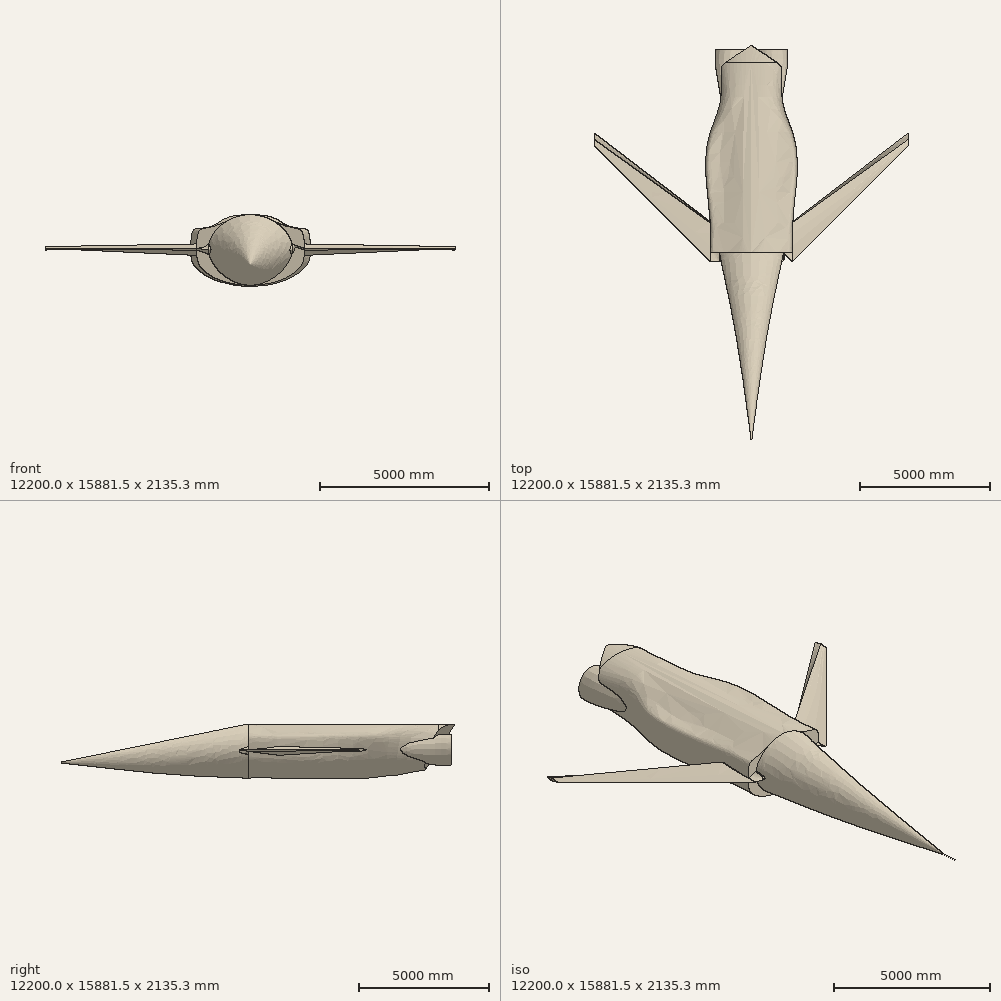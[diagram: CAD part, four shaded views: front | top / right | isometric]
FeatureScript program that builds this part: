
annotation { "Feature Type Name" : "Feature", "Feature Type Description" : "" }
export const myFeature = defineFeature(function(context is Context, id is Id, definition is map)
    precondition{}
    {
        {
            var Q0;
            Q0=qCreatedBy(makeId("Right.planeOp"),FACE);
            var sketch = newSketch(context, id + "F0", { "sketchPlane" : qUnion([Q0])});
            skLineSegment(sketch, "E0", {"start": v(0, 0) * mm, "end": v(-1750, 0) * mm});
            skLineSegment(sketch, "E1", {"start": v(-1750, 0) * mm, "end": v(-3500, 0) * mm});
            skLineSegment(sketch, "E2", {"start": v(-3500, 0) * mm, "end": v(-3500, -1000) * mm});
            skLineSegment(sketch, "E3", {"start": v(-3500, -1000) * mm, "end": v(-8500, -1000) * mm});
            skLineSegment(sketch, "E4", {"start": v(-8500, -1000) * mm, "end": v(-8500, -499.31) * mm});
            skLineSegment(sketch, "E5", {"start": v(-1151.4, 0) * mm, "end": v(-1151.4, 1000) * mm});
            skLineSegment(sketch, "E6", {"start": v(-1151.4, 1000) * mm, "end": v(-8500, -499.31) * mm});
            skLineSegment(sketch, "E7", {"start": v(-8500, -499.31) * mm, "end": v(-3500, -1000) * mm});
            skLineSegment(sketch, "E8", {"start": v(-3500, 0) * mm, "end": v(-3500, 520.82) * mm});
            skLineSegment(sketch, "E9", {"start": v(-8500, -499.31) * mm, "end": v(-8450, -499.31) * mm});
            skLineSegment(sketch, "E10", {"start": v(-8450, -499.31) * mm, "end": v(-8450, -489.1) * mm});
            skLineSegment(sketch, "E11", {"start": v(-8450, -499.31) * mm, "end": v(-8450, -504.32) * mm});
            skSolve(sketch);
        }
        {
            var Q0;
            Q0=sQuery(id+"F0.wireOp",EDGE,"E5");
            cPlane(context, id + "F1", {"entities" : qUnion([Q0]), "cplaneType" : CPlaneType.LINE_ANGLE, "offset" : 25 * mm, "angle" : 90 * degree, "oppositeDirection" : true, "width" : 150 * mm, "height" : 150 * mm});
        }
        {
            var Q0;
            Q0=qCreatedBy(id+"F1.planeOp",FACE);
            var sketch = newSketch(context, id + "F2", { "sketchPlane" : qUnion([Q0])});
            skPoint(sketch, "E12.middle", {"position": v(0, 0) * mm});
            skFitSpline(sketch, "E13", {"points": [v(0, 1000) * mm, v(-1060, 662.5) * mm, v(-1517.6, 506.84) * mm, v(-1600, 0) * mm, v(-1517.6, -506.84) * mm, v(-750, -1000) * mm, v(750, -1000) * mm, v(1517.6, -506.84) * mm, v(1600, 0) * mm, v(1517.6, 506.84) * mm, v(1060, 662.5) * mm, v(0, 1000) * mm]});
            skSolve(sketch);
        }
        {
            var Q0;
            Q0=qCreatedBy(makeId("Front.planeOp"),FACE);
            var sketch = newSketch(context, id + "F3", { "sketchPlane" : qUnion([Q0])});
            skPoint(sketch, "E14.middle", {"position": v(0, 0) * mm});
            skFitSpline(sketch, "E15", {"points": [v(0, 1000) * mm, v(-1060, 662.5) * mm, v(-1517.6, 506.84) * mm, v(-1600, 0) * mm, v(-1517.6, -506.84) * mm, v(-750, -1000) * mm, v(750, -1000) * mm, v(1517.6, -506.84) * mm, v(1600, 0) * mm, v(1517.6, 506.84) * mm, v(1060, 662.5) * mm, v(0, 1000) * mm]});
            skSolve(sketch);
        }
        {
            var Q0;
            Q0=qCreatedBy(makeId("Front.planeOp"),FACE);
            cPlane(context, id + "F4", {"entities" : qUnion([Q0]), "cplaneType" : CPlaneType.OFFSET, "offset" : 3500 * mm, "oppositeDirection" : true, "width" : 150 * mm, "height" : 150 * mm});
        }
        {
            var Q0;
            Q0=qCreatedBy(id+"F4.planeOp",FACE);
            var sketch = newSketch(context, id + "F5", { "sketchPlane" : qUnion([Q0])});
            skPoint(sketch, "E16.middle", {"position": v(0, 0) * mm});
            skFitSpline(sketch, "E17", {"points": [v(0, 1000) * mm, v(-1060, 662.5) * mm, v(-1517.6, 506.84) * mm, v(-1600, 0) * mm, v(-1517.6, -506.84) * mm, v(-750, -1000) * mm, v(750, -1000) * mm, v(1517.6, -506.84) * mm, v(1600, 0) * mm, v(1517.6, 506.84) * mm, v(1060, 662.5) * mm, v(0, 1000) * mm]});
            skSolve(sketch);
        }
        {
            var Q0;
            Q0=qCreatedBy(makeId("Front.planeOp"),FACE);
            cPlane(context, id + "F6", {"entities" : qUnion([Q0]), "cplaneType" : CPlaneType.OFFSET, "offset" : 4500 * mm, "oppositeDirection" : true, "width" : 150 * mm, "height" : 150 * mm});
        }
        {
            var Q0;
            Q0=qCreatedBy(id+"F6.planeOp",FACE);
            var sketch = newSketch(context, id + "F7", { "sketchPlane" : qUnion([Q0])});
            skPoint(sketch, "E18.middle", {"position": v(0, 0) * mm});
            skFitSpline(sketch, "E19", {"points": [v(0, 1000) * mm, v(-1060, 662.5) * mm, v(-1250, 0) * mm, v(-1060, -662.5) * mm, v(0, -1000) * mm, v(1060, -662.5) * mm, v(1250, 0) * mm, v(1060, 662.5) * mm, v(0, 1000) * mm]});
            skSolve(sketch);
        }
        {
            var Q0;
            Q0=qCreatedBy(makeId("Front.planeOp"),FACE);
            cPlane(context, id + "F8", {"entities" : qUnion([Q0]), "cplaneType" : CPlaneType.OFFSET, "offset" : 6232.05 * mm, "oppositeDirection" : true, "width" : 150 * mm, "height" : 150 * mm});
        }
        {
            var Q0;
            Q0=qCreatedBy(id+"F8.planeOp",FACE);
            var sketch = newSketch(context, id + "F9", { "sketchPlane" : qUnion([Q0])});
            skPoint(sketch, "E20.middle", {"position": v(0, 0) * mm});
            skFitSpline(sketch, "E21", {"points": [v(0, 1000) * mm, v(-1060, 662.5) * mm, v(-1250, 0) * mm, v(-848, -530) * mm, v(848, -530) * mm, v(1250, 0) * mm, v(1060, 662.5) * mm, v(0, 1000) * mm]});
            skSolve(sketch);
        }
        {
            var Q0;
            Q0=makeQuery(id+"F2.imprint","IMPRINT",FACE,{"disambiguationData":[TD([[makeQuery(id+"F2.imprint","IMPRINT",EDGE,{"derivedFrom":sQuery(id+"F2.wireOp",EDGE,"E13")}),1.0]])]});
            var Q1;
            Q1=makeQuery(id+"F3.imprint","IMPRINT",FACE,{"disambiguationData":[TD([[makeQuery(id+"F3.imprint","IMPRINT",EDGE,{"derivedFrom":sQuery(id+"F3.wireOp",EDGE,"E15")}),1.0]])]});
            var Q2;
            Q2=makeQuery(id+"F5.imprint","IMPRINT",FACE,{"disambiguationData":[TD([[makeQuery(id+"F5.imprint","IMPRINT",EDGE,{"derivedFrom":sQuery(id+"F5.wireOp",EDGE,"E17")}),1.0]])]});
            var Q3;
            Q3=makeQuery(id+"F7.imprint","IMPRINT",FACE,{"disambiguationData":[TD([[makeQuery(id+"F7.imprint","IMPRINT",EDGE,{"derivedFrom":sQuery(id+"F7.wireOp",EDGE,"E19")}),1.0]])]});
            var Q4;
            Q4=makeQuery(id+"F9.imprint","IMPRINT",FACE,{"disambiguationData":[TD([[makeQuery(id+"F9.imprint","IMPRINT",EDGE,{"derivedFrom":sQuery(id+"F9.wireOp",EDGE,"E21")}),1.0]])]});
            loft(context, id + "F10", {"sheetProfilesArray" : [{ "sheetProfileEntities" : qUnion([Q0]) }, { "sheetProfileEntities" : qUnion([Q1]) }, { "sheetProfileEntities" : qUnion([Q2]) }, { "sheetProfileEntities" : qUnion([Q3]) }, { "sheetProfileEntities" : qUnion([Q4]) }]});
        }
        {
            var Q0;
            Q0=makeQuery(id+"F10.opLoft","CAP_FACE",FACE,{"disambiguationData":[OSD([makeQuery(id+"F9.imprint","IMPRINT",FACE,{"disambiguationData":[TD([[makeQuery(id+"F9.imprint","IMPRINT",EDGE,{"derivedFrom":sQuery(id+"F9.wireOp",EDGE,"E21")}),1.0]])]})])],"isStart":true});
            extrude(context, id + "F11", {"entities" : qUnion([Q0]), "operationType" : NewBodyOperationType.ADD, "depth" : 649.4 * mm, "offsetDistance" : 25 * mm});
        }
        {
            var Q0;
            Q0=qCreatedBy(makeId("Right.planeOp"),FACE);
            var sketch = newSketch(context, id + "F12", { "sketchPlane" : qUnion([Q0])});
            skLineSegment(sketch, "E22", {"start": v(0, 0) * mm, "end": v(4500, 0) * mm});
            skLineSegment(sketch, "E23", {"start": v(4500, 0) * mm, "end": v(6232.05, 0) * mm});
            skLineSegment(sketch, "E24", {"start": v(4500, 0) * mm, "end": v(4500, 1000) * mm});
            skLineSegment(sketch, "E25", {"start": v(4500, 1000) * mm, "end": v(6881.46, 1000) * mm});
            skLineSegment(sketch, "E26", {"start": v(6881.46, 1000) * mm, "end": v(6881.46, -1000) * mm});
            skLineSegment(sketch, "E27", {"start": v(6881.46, 1000) * mm, "end": v(6232.05, 0) * mm});
            skLineSegment(sketch, "E28", {"start": v(6232.05, 0) * mm, "end": v(5582.64, -1000) * mm});
            skLineSegment(sketch, "E29", {"start": v(5582.64, -1000) * mm, "end": v(6881.46, -1000) * mm});
            skSolve(sketch);
        }
        {
            var Q0;
            Q0=makeQuery(id+"F12.imprint","IMPRINT",FACE,{"disambiguationData":[TD([[makeQuery(id+"F12.imprint","IMPRINT",EDGE,{"derivedFrom":sQuery(id+"F12.wireOp",EDGE,"E26")}),-1.0]])]});
            var Q1;
            Q1=sQuery(id+"F12.wireOp",EDGE,"E25");
            revolve(context, id + "F13", {"operationType" : NewBodyOperationType.REMOVE, "entities" : qUnion([Q0]), "axis" : qUnion([Q1]), "revolveType" : RevolveType.SYMMETRIC, "oppositeDirection" : true, "angle" : 182 * degree});
        }
        {
            var Q0;
            Q0=qCreatedBy(id+"F1.planeOp",FACE);
            var sketch = newSketch(context, id + "F14", { "sketchPlane" : qUnion([Q0])});
            skFitSpline(sketch, "E30", {"points": [v(0, 1000) * mm, v(-1250, 0) * mm, v(0, -1099.92) * mm, v(1250, 0) * mm, v(0, 1000) * mm]});
            skSolve(sketch);
        }
        {
            var Q0;
            Q0=qCreatedBy(makeId("Front.planeOp"),FACE);
            cPlane(context, id + "F15", {"entities" : qUnion([Q0]), "cplaneType" : CPlaneType.OFFSET, "offset" : 3500 * mm, "width" : 150 * mm, "height" : 150 * mm});
        }
        {
            var Q0;
            Q0=qCreatedBy(id+"F15.planeOp",FACE);
            var sketch = newSketch(context, id + "F16", { "sketchPlane" : qUnion([Q0])});
            skCircle(sketch, "E31", {"center": v(0, -239.59) * mm, "radius": 760.41 * mm});
            skSolve(sketch);
        }
        {
            var Q0;
            Q0=qCreatedBy(makeId("Front.planeOp"),FACE);
            cPlane(context, id + "F17", {"entities" : qUnion([Q0]), "cplaneType" : CPlaneType.OFFSET, "offset" : 8450 * mm, "width" : 150 * mm, "height" : 150 * mm});
        }
        {
            var Q0;
            Q0=qCreatedBy(id+"F17.planeOp",FACE);
            var sketch = newSketch(context, id + "F18", { "sketchPlane" : qUnion([Q0])});
            skCircle(sketch, "E32", {"center": v(0, -496.71) * mm, "radius": 7.6 * mm});
            skSolve(sketch);
        }
        {
            var Q1;
            Q1=makeQuery(id+"F18.imprint","IMPRINT",FACE,{"disambiguationData":[TD([[makeQuery(id+"F18.imprint","IMPRINT",EDGE,{"derivedFrom":sQuery(id+"F18.wireOp",EDGE,"E32")}),1.0]])]});
            var Q2;
            Q2=makeQuery(id+"F16.imprint","IMPRINT",FACE,{"disambiguationData":[TD([[makeQuery(id+"F16.imprint","IMPRINT",EDGE,{"derivedFrom":sQuery(id+"F16.wireOp",EDGE,"E31")}),1.0]])]});
            var Q3;
            Q3=makeQuery(id+"F14.imprint","IMPRINT",FACE,{"disambiguationData":[TD([[makeQuery(id+"F14.imprint","IMPRINT",EDGE,{"derivedFrom":sQuery(id+"F14.wireOp",EDGE,"E30")}),1.0]])]});
            loft(context, id + "F19", {"operationType" : NewBodyOperationType.ADD, "sheetProfilesArray" : [{ "sheetProfileEntities" : qUnion([Q1]) }, { "sheetProfileEntities" : qUnion([Q2]) }, { "sheetProfileEntities" : qUnion([Q3]) }]});
        }
        {
            var Q0;
            Q0=makeQuery(id+"F19.opLoft","CAP_FACE",FACE,{"disambiguationData":[OSD([makeQuery(id+"F18.imprint","IMPRINT",FACE,{"disambiguationData":[TD([[makeQuery(id+"F18.imprint","IMPRINT",EDGE,{"derivedFrom":sQuery(id+"F18.wireOp",EDGE,"E32")}),1.0]])]})])],"isStart":true});
            extrude(context, id + "F20", {"entities" : qUnion([Q0]), "operationType" : NewBodyOperationType.ADD, "depth" : 550 * mm, "offsetDistance" : 25 * mm});
        }
        {
            var Q0;
            Q0=qCreatedBy(makeId("Front.planeOp"),FACE);
            cPlane(context, id + "F21", {"entities" : qUnion([Q0]), "cplaneType" : CPlaneType.OFFSET, "offset" : 3500 * mm, "oppositeDirection" : true, "width" : 150 * mm, "height" : 150 * mm});
        }
        {
            var Q0;
            Q0=qCreatedBy(id+"F21.planeOp",FACE);
            var sketch = newSketch(context, id + "F22", { "sketchPlane" : qUnion([Q0])});
            skCircle(sketch, "E33", {"center": v(-800, 0) * mm, "radius": 600 * mm});
            skCircle(sketch, "E34", {"center": v(800, 0) * mm, "radius": 600 * mm});
            skSolve(sketch);
        }
        {
            var Q0;
            Q0=qCreatedBy(makeId("Front.planeOp"),FACE);
            cPlane(context, id + "F23", {"entities" : qUnion([Q0]), "cplaneType" : CPlaneType.OFFSET, "offset" : 4500 * mm, "oppositeDirection" : true, "width" : 150 * mm, "height" : 150 * mm});
        }
        {
            var Q0;
            Q0=qCreatedBy(id+"F23.planeOp",FACE);
            var sketch = newSketch(context, id + "F24", { "sketchPlane" : qUnion([Q0])});
            skCircle(sketch, "E35", {"center": v(-800, 0) * mm, "radius": 400 * mm});
            skCircle(sketch, "E36", {"center": v(800, 0) * mm, "radius": 400 * mm});
            skSolve(sketch);
        }
        {
            var Q0;
            Q0=qCreatedBy(makeId("Front.planeOp"),FACE);
            cPlane(context, id + "F25", {"entities" : qUnion([Q0]), "cplaneType" : CPlaneType.OFFSET, "offset" : 6232.05 * mm, "oppositeDirection" : true, "width" : 150 * mm, "height" : 150 * mm});
        }
        {
            var Q0;
            Q0=qCreatedBy(id+"F25.planeOp",FACE);
            var sketch = newSketch(context, id + "F26", { "sketchPlane" : qUnion([Q0])});
            skCircle(sketch, "E37", {"center": v(-800, 0) * mm, "radius": 600 * mm});
            skCircle(sketch, "E38", {"center": v(800, 0) * mm, "radius": 600 * mm});
            skSolve(sketch);
        }
        {
            var Q0;
            Q0=qCreatedBy(makeId("Front.planeOp"),FACE);
            cPlane(context, id + "F27", {"entities" : qUnion([Q0]), "cplaneType" : CPlaneType.OFFSET, "offset" : 6732.05 * mm, "oppositeDirection" : true, "width" : 150 * mm, "height" : 150 * mm});
        }
        {
            var Q0;
            Q0=qCreatedBy(id+"F27.planeOp",FACE);
            var sketch = newSketch(context, id + "F28", { "sketchPlane" : qUnion([Q0])});
            skCircle(sketch, "E39", {"center": v(-800, 0) * mm, "radius": 600 * mm});
            skCircle(sketch, "E40", {"center": v(800, 0) * mm, "radius": 600 * mm});
            skSolve(sketch);
        }
        {
            var Q0;
            Q0=makeQuery(id+"F22.imprint","IMPRINT",FACE,{"disambiguationData":[TD([[makeQuery(id+"F22.imprint","IMPRINT",EDGE,{"derivedFrom":sQuery(id+"F22.wireOp",EDGE,"E33")}),1.0]])]});
            var Q1;
            Q1=makeQuery(id+"F24.imprint","IMPRINT",FACE,{"disambiguationData":[TD([[makeQuery(id+"F24.imprint","IMPRINT",EDGE,{"derivedFrom":sQuery(id+"F24.wireOp",EDGE,"E35")}),1.0]])]});
            var Q2;
            Q2=makeQuery(id+"F26.imprint","IMPRINT",FACE,{"disambiguationData":[TD([[makeQuery(id+"F26.imprint","IMPRINT",EDGE,{"derivedFrom":sQuery(id+"F26.wireOp",EDGE,"E37")}),1.0]])]});
            var Q3;
            Q3=makeQuery(id+"F28.imprint","IMPRINT",FACE,{"disambiguationData":[TD([[makeQuery(id+"F28.imprint","IMPRINT",EDGE,{"derivedFrom":sQuery(id+"F28.wireOp",EDGE,"E39")}),1.0]])]});
            loft(context, id + "F29", {"sheetProfilesArray" : [{ "sheetProfileEntities" : qUnion([Q0]) }, { "sheetProfileEntities" : qUnion([Q1]) }, { "sheetProfileEntities" : qUnion([Q2]) }, { "sheetProfileEntities" : qUnion([Q3]) }]});
        }
        {
            var Q0;
            Q0=makeQuery(id+"F22.imprint","IMPRINT",FACE,{"disambiguationData":[TD([[makeQuery(id+"F22.imprint","IMPRINT",EDGE,{"derivedFrom":sQuery(id+"F22.wireOp",EDGE,"E34")}),1.0]])]});
            var Q1;
            Q1=makeQuery(id+"F24.imprint","IMPRINT",FACE,{"disambiguationData":[TD([[makeQuery(id+"F24.imprint","IMPRINT",EDGE,{"derivedFrom":sQuery(id+"F24.wireOp",EDGE,"E36")}),1.0]])]});
            var Q2;
            Q2=makeQuery(id+"F26.imprint","IMPRINT",FACE,{"disambiguationData":[TD([[makeQuery(id+"F26.imprint","IMPRINT",EDGE,{"derivedFrom":sQuery(id+"F26.wireOp",EDGE,"E38")}),1.0]])]});
            var Q3;
            Q3=makeQuery(id+"F28.imprint","IMPRINT",FACE,{"disambiguationData":[TD([[makeQuery(id+"F28.imprint","IMPRINT",EDGE,{"derivedFrom":sQuery(id+"F28.wireOp",EDGE,"E40")}),1.0]])]});
            loft(context, id + "F30", {"sheetProfilesArray" : [{ "sheetProfileEntities" : qUnion([Q0]) }, { "sheetProfileEntities" : qUnion([Q1]) }, { "sheetProfileEntities" : qUnion([Q2]) }, { "sheetProfileEntities" : qUnion([Q3]) }]});
        }
        {
            var Q0;
            Q0=qCreatedBy(makeId("Right.planeOp"),FACE);
            var sketch = newSketch(context, id + "F31", { "sketchPlane" : qUnion([Q0])});
            skFitSpline(sketch, "E41", {"points": [v(-1500, -50) * mm, v(0, 250) * mm, v(3000, -50) * mm, v(0, -250) * mm, v(-1500, -50) * mm]});
            skSolve(sketch);
        }
        {
            var Q0;
            Q0=qCreatedBy(makeId("Right.planeOp"),FACE);
            cPlane(context, id + "F32", {"entities" : qUnion([Q0]), "cplaneType" : CPlaneType.OFFSET, "offset" : 1600 * mm, "oppositeDirection" : true, "width" : 150 * mm, "height" : 150 * mm});
        }
        {
            var Q0;
            Q0=qCreatedBy(id+"F32.planeOp",FACE);
            var sketch = newSketch(context, id + "F33", { "sketchPlane" : qUnion([Q0])});
            skFitSpline(sketch, "E42", {"points": [v(-1500, 0) * mm, v(1000, 250) * mm, v(3500, 0) * mm], "startDerivative": vector(7500, 0) * mm, "endDerivative": vector(7500, 0) * mm});
            skFitSpline(sketch, "E43", {"points": [v(-1500, 0) * mm, v(1000, -250) * mm, v(3500, 0) * mm], "startDerivative": vector(5000, -750) * mm, "endDerivative": vector(7500, 0) * mm});
            skSolve(sketch);
        }
        {
            var Q0;
            Q0=qCreatedBy(makeId("Right.planeOp"),FACE);
            cPlane(context, id + "F34", {"entities" : qUnion([Q0]), "cplaneType" : CPlaneType.OFFSET, "offset" : 1600 * mm, "width" : 150 * mm, "height" : 150 * mm});
        }
        {
            var Q0;
            Q0=qCreatedBy(id+"F34.planeOp",FACE);
            var sketch = newSketch(context, id + "F35", { "sketchPlane" : qUnion([Q0])});
            skFitSpline(sketch, "E44", {"points": [v(-1500, 0) * mm, v(1000, 250) * mm, v(3500, 0) * mm], "startDerivative": vector(7500, 0) * mm, "endDerivative": vector(7500, 0) * mm});
            skFitSpline(sketch, "E45", {"points": [v(-1500, 0) * mm, v(1000, -250) * mm, v(3500, 0) * mm], "startDerivative": vector(5000, -750) * mm, "endDerivative": vector(7500, 0) * mm});
            skSolve(sketch);
        }
        {
            var Q0;
            Q0=qCreatedBy(makeId("Right.planeOp"),FACE);
            cPlane(context, id + "F36", {"entities" : qUnion([Q0]), "cplaneType" : CPlaneType.OFFSET, "offset" : 6100 * mm, "oppositeDirection" : true, "width" : 150 * mm, "height" : 150 * mm});
        }
        {
            var Q0;
            Q0=qCreatedBy(id+"F36.planeOp",FACE);
            var sketch = newSketch(context, id + "F37", { "sketchPlane" : qUnion([Q0])});
            skFitSpline(sketch, "E46", {"points": [v(3000, 0) * mm, v(3250, 50) * mm, v(3500, 0) * mm], "startDerivative": vector(750, 0) * mm, "endDerivative": vector(750, 0) * mm});
            skFitSpline(sketch, "E47", {"points": [v(3000, 0) * mm, v(3250, -50) * mm, v(3500, 0) * mm], "startDerivative": vector(500, -150) * mm, "endDerivative": vector(750, 0) * mm});
            skSolve(sketch);
        }
        {
            var Q0;
            Q0=qCreatedBy(makeId("Right.planeOp"),FACE);
            cPlane(context, id + "F38", {"entities" : qUnion([Q0]), "cplaneType" : CPlaneType.OFFSET, "offset" : 6100 * mm, "width" : 150 * mm, "height" : 150 * mm});
        }
        {
            var Q0;
            Q0=qCreatedBy(id+"F38.planeOp",FACE);
            var sketch = newSketch(context, id + "F39", { "sketchPlane" : qUnion([Q0])});
            skFitSpline(sketch, "E48", {"points": [v(3000, 0) * mm, v(3250, 50) * mm, v(3500, 0) * mm], "startDerivative": vector(750, 0) * mm, "endDerivative": vector(750, 0) * mm});
            skFitSpline(sketch, "E49", {"points": [v(3000, 0) * mm, v(3250, -50) * mm, v(3500, 0) * mm], "startDerivative": vector(500, -150) * mm, "endDerivative": vector(750, 0) * mm});
            skSolve(sketch);
        }
        {
            var Q0;
            Q0=qSketchRegion(id+"F31",true);
            extrude(context, id + "F40", {"entities" : qUnion([Q0]), "endBound" : BoundingType.SYMMETRIC, "depth" : 2500 * mm, "offsetDistance" : 25 * mm});
        }
        {
            var Q1;
            Q1=makeQuery(id+"F40.opExtrude","CAP_FACE",FACE,{"disambiguationData":[OSD([sQuery(id+"F31.wireOp",EDGE,"E41")])],"isStart":true});
            var Q2;
            {var subQ0=sQuery(id+"F33.wireOp",EDGE,"E42");Q2=makeQuery(id+"F33.imprint","IMPRINT",FACE,{"disambiguationData":[TD([[makeQuery(id+"F33.imprint","IMPRINT",EDGE,{"derivedFrom":subQ0}),-1.0]])]});}
            loft(context, id + "F41", {"operationType" : NewBodyOperationType.ADD, "sheetProfilesArray" : [{ "sheetProfileEntities" : qUnion([Q1]) }, { "sheetProfileEntities" : qUnion([Q2]) }]});
        }
        {
            var Q1;
            Q1=makeQuery(id+"F40.opExtrude","CAP_FACE",FACE,{"disambiguationData":[OSD([sQuery(id+"F31.wireOp",EDGE,"E41")])],"isStart":false});
            var Q2;
            {var subQ0=sQuery(id+"F35.wireOp",EDGE,"E44");Q2=makeQuery(id+"F35.imprint","IMPRINT",FACE,{"disambiguationData":[TD([[makeQuery(id+"F35.imprint","IMPRINT",EDGE,{"derivedFrom":subQ0}),-1.0]])]});}
            loft(context, id + "F42", {"operationType" : NewBodyOperationType.ADD, "sheetProfilesArray" : [{ "sheetProfileEntities" : qUnion([Q1]) }, { "sheetProfileEntities" : qUnion([Q2]) }]});
        }
        {
            var Q1;
            {var subQ0=sQuery(id+"F33.wireOp",EDGE,"E42");Q1=makeQuery(id+"F41.opLoft","CAP_FACE",FACE,{"disambiguationData":[OSD([makeQuery(id+"F33.imprint","IMPRINT",FACE,{"disambiguationData":[TD([[makeQuery(id+"F33.imprint","IMPRINT",EDGE,{"derivedFrom":subQ0}),-1.0]])]})])],"isStart":true});}
            var Q2;
            {var subQ0=sQuery(id+"F37.wireOp",EDGE,"E46");Q2=makeQuery(id+"F37.imprint","IMPRINT",FACE,{"disambiguationData":[TD([[makeQuery(id+"F37.imprint","IMPRINT",EDGE,{"derivedFrom":subQ0}),-1.0]])]});}
            loft(context, id + "F43", {"operationType" : NewBodyOperationType.ADD, "sheetProfilesArray" : [{ "sheetProfileEntities" : qUnion([Q1]) }, { "sheetProfileEntities" : qUnion([Q2]) }]});
        }
        {
            var Q1;
            {var subQ0=sQuery(id+"F35.wireOp",EDGE,"E44");Q1=makeQuery(id+"F42.opLoft","CAP_FACE",FACE,{"disambiguationData":[OSD([makeQuery(id+"F35.imprint","IMPRINT",FACE,{"disambiguationData":[TD([[makeQuery(id+"F35.imprint","IMPRINT",EDGE,{"derivedFrom":subQ0}),-1.0]])]})])],"isStart":true});}
            var Q2;
            {var subQ0=sQuery(id+"F39.wireOp",EDGE,"E48");Q2=makeQuery(id+"F39.imprint","IMPRINT",FACE,{"disambiguationData":[TD([[makeQuery(id+"F39.imprint","IMPRINT",EDGE,{"derivedFrom":subQ0}),-1.0]])]});}
            loft(context, id + "F44", {"operationType" : NewBodyOperationType.ADD, "sheetProfilesArray" : [{ "sheetProfileEntities" : qUnion([Q1]) }, { "sheetProfileEntities" : qUnion([Q2]) }]});
        }
    });
